# Revit family: Seals-Shelters_Serco_S-2200
name_source: partatom
category: Generic Models
units: mm (PartAtom-declared; Revit-internal decimal feet)

## family parameters
Always vertical = Yes
Can host rebar = No
Cut with Voids When Loaded = No
Host = Wall
Maintain Annotation Orientation = No
Part Type = Normal
Room Calculation Point = No
Round Connector Dimension = Use Diameter
Shared = No

## types (4) — shared parameters
Default Elevation = 0' - 0"
Description = Foamside Dock Shelter
DropCurtain = 3' - 0"
Manufacturer = Entrematic
Model = S-2200 Ultra Dock (FSR-1000 Foamside)
Opening = 7' - 6"
URL = https://www.entrematic.us

## per-type parameters (varying)
| type | CurtainW | Height | Projection | Width |
| 11'-6" x 11', Standard Projection | 10' - 6" | 11' - 0" | 1' - 6" | 11' - 6" |
| 11'-6" x 11', Swing-In Projection | 10' - 6" | 11' - 0" | 2' - 4" | 11' - 6" |
| 12'-6" x 12'-6", Swing-In Projection | 11' - 6" | 12' - 6" | 2' - 4" | 12' - 6" |
| 12'-6" x 12'-6", Standard Projection | 11' - 6" | 12' - 6" | 1' - 6" | 12' - 6" |

## geometry (parser evidence)
native form markers: Sweep x3
no freeform markers — native parametric forms only
